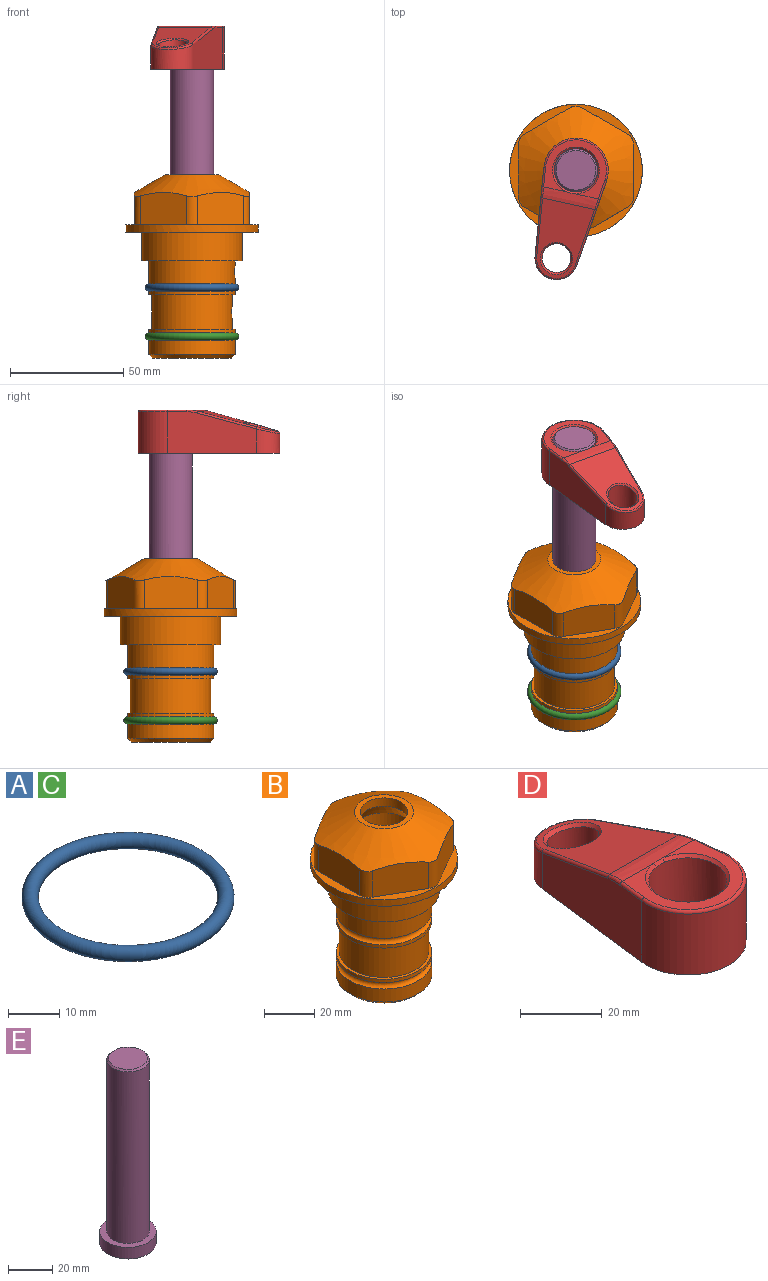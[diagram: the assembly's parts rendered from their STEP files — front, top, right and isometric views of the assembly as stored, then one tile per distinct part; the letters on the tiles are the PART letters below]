
ASSEMBLY  parts=5 mates=4
PART A: 1 faces, bbox 44.7x44.7x3.2 mm
  f0: torus R=19.05mm, axis (0,0,1), area 1193.9mm2
PART B: 36 faces, bbox 58.7x58.7x81 mm
  f0: cylinder r=17.78mm len=35.56mm, axis (0,0,1), area 1670.8mm2, adj f23,f24,f31
  f1: cylinder r=19.05mm len=38.1mm, axis (0,0,1), area 1191.9mm2, adj f26,f27,f30
  f2: plane 58.66x58.66mm, normal (0,0,-1), area 1150.6mm2, adj f3,f28
  f3: cylinder r=29.33mm len=58.66mm, axis (0,0,-1), area 585.1mm2, adj f2,f4
  f4: plane 58.66x58.66mm, normal (0,0,1), area 475.9mm2, adj f3,f5,f6,f7,f8,f9,f10,f11
  f5: plane 20.32x14.34mm, normal (-0.5,0.87,0), area 324.4mm2, adj f4,f15,f16,f17
  f6: plane 20.32x14.34mm, normal (0.5,0.87,0), area 324.4mm2, adj f4,f14,f15,f17
  f7: plane 23.48x14.34mm, normal (1,0,0), area 324.4mm2, adj f4,f13,f14,f17
  f8: plane 20.32x14.34mm, normal (0.5,-0.87,0), area 324.4mm2, adj f4,f12,f13,f17
  f9: plane 20.32x14.34mm, normal (-0.5,-0.87,0), area 324.4mm2, adj f4,f11,f12,f17
  f10: plane 23.48x14.34mm, normal (-1,0,0), area 324.4mm2, adj f4,f11,f16,f17
  f11: cylinder r=5.08mm len=12.85mm, axis (0,0,-1), area 67.2mm2, adj f4,f9,f10,f17
  f12: cylinder r=5.08mm len=12.85mm, axis (0,0,-1), area 67.2mm2, adj f4,f8,f9,f17
  f13: cylinder r=5.08mm len=12.85mm, axis (0,0,-1), area 67.2mm2, adj f4,f7,f8,f17
  f14: cylinder r=5.08mm len=12.85mm, axis (0,0,-1), area 67.2mm2, adj f4,f6,f7,f17
  f15: cylinder r=5.08mm len=12.85mm, axis (0,0,-1), area 67.2mm2, adj f4,f5,f6,f17
  f16: cylinder r=5.08mm len=12.85mm, axis (0,0,-1), area 67.2mm2, adj f4,f5,f10,f17
  f17: cone r=11.73mm half-angle=60deg, axis (0,0,-1), area 2071.8mm2, adj f5,f6,f7,f8,f9,f10,f11,f12
  f18: plane 23.46x23.46mm, normal (0,0,1), area 147.4mm2, adj f17,f35
  f19: plane 34.93x34.93mm, normal (0,0,-1), area 958mm2, adj f29
  f20: cylinder r=19.05mm len=38.1mm, axis (0,0,1), area 760.1mm2, adj f21,f29
  f21: torus R=19.05mm, axis (0,0,1), area 565.3mm2, adj f20,f22
  f22: cylinder r=19.05mm len=38.1mm, axis (0,0,1), area 190mm2, adj f21,f23
  f23: plane 38.1x38.1mm, normal (0,0,1), area 146.9mm2, adj f0,f22
  f24: plane 38.1x38.1mm, normal (0,0,-1), area 146.9mm2, adj f0,f25
  f25: cylinder r=19.05mm len=38.1mm, axis (0,0,1), area 190mm2, adj f24,f26
  f26: torus R=19.05mm, axis (0,0,1), area 565.3mm2, adj f1,f25
  f27: plane 44.45x44.45mm, normal (0,0,-1), area 411.7mm2, adj f1,f28
  f28: cylinder r=22.23mm len=44.45mm, axis (0,0,1), area 1773.5mm2, adj f2,f27
  f29: cone r=19.05mm half-angle=45deg, axis (0,0,1), area 257.5mm2, adj f19,f20
  f30: cylinder r=3.17mm len=6.75mm, axis (-1,0,0), area 128mm2, adj f1,f33
  f31: cylinder r=3.17mm len=6.35mm, axis (-1,0,0), area 102.5mm2, adj f0,f33
  f32: plane 25.4x25.4mm, normal (0,0,1), area 506.7mm2, adj f33
  f33: cylinder r=12.7mm len=66.42mm, axis (0,0,-1), area 5236.2mm2, adj f30,f31,f32,f34
  f34: cone r=9.53mm half-angle=30deg, axis (0,0,-1), area 443.4mm2, adj f33,f35
  f35: cylinder r=9.53mm len=19.05mm, axis (0,0,-1), area 240.9mm2, adj f18,f34
PART C: same geometry as A
PART D: 31 faces, bbox 31.7x65.5x19.8 mm
  f0: plane 39.12x18.26mm, normal (0.99,0.12,0), area 612.2mm2, adj f1,f4,f7,f11,f13,f15
  f1: cylinder r=9.53mm len=18.91mm, axis (0,0,-1), area 296.1mm2, adj f0,f2,f7,f17
  f2: plane 39.12x18.26mm, normal (-0.99,0.12,0), area 612.2mm2, adj f1,f4,f7,f12,f14,f16
  f3: cylinder r=6.35mm len=12.7mm, axis (0,0,-1), area 362.4mm2, adj f7,f18
  f4: cylinder r=14.29mm len=28.58mm, axis (0,0,-1), area 882.2mm2, adj f0,f2,f7,f10
  f5: cylinder r=9.53mm len=19.05mm, axis (0,0,-1), area 1092.6mm2, adj f7,f19,f20
  f6: plane 26.99x23.69mm, normal (0,0,1), area 216.2mm2, adj f9,f10,f11,f12,f19
  f7: plane 63.5x28.58mm, normal (0,0,-1), area 661.8mm2, adj f0,f1,f2,f3,f4,f5,f22,f23
  f8: plane 33.52x23.6mm, normal (0,0.26,0.97), area 486mm2, adj f9,f15,f16,f17,f18
  f9: cylinder r=19.05mm len=24.72mm, axis (1,0,0), area 120.4mm2, adj f6,f8,f13,f14,f20
  f10: torus R=13.49mm, axis (0,0,1), area 59mm2, adj f4,f6,f11,f12
  f11: cylinder r=0.79mm len=8.67mm, axis (0.12,-0.99,0), area 10.8mm2, adj f0,f6,f10,f13
  f12: cylinder r=0.79mm len=8.67mm, axis (0.12,0.99,0), area 10.8mm2, adj f2,f6,f10,f14
  f13: bspline ~4.95x1.42mm, area 6.1mm2, adj f0,f9,f11,f15
  f14: bspline ~4.95x1.42mm, area 6.1mm2, adj f2,f9,f12,f16
  f15: cylinder r=0.79mm len=25.95mm, axis (0.12,-0.96,0.26), area 32.9mm2, adj f0,f8,f13,f17
  f16: cylinder r=0.79mm len=25.95mm, axis (0.12,0.96,-0.26), area 32.9mm2, adj f2,f8,f14,f17
  f17: bspline ~18.91x8.38mm, area 30mm2, adj f1,f8,f15,f16
  f18: bspline ~14.29x14.29mm, area 48.3mm2, adj f3,f8
  f19: cone r=9.53mm half-angle=45deg, axis (0,0,1), area 66.5mm2, adj f5,f6,f20
  f20: bspline ~3.22x0.96mm, area 3.5mm2, adj f5,f9,f19
  f21: plane 2.75x2.72mm, normal (0,0,-1), area 2.9mm2, adj f23,f25,f28
  f22: plane 23.05x15.88mm, normal (-0.99,-0.12,0), area 323.6mm2, adj f7,f25,f26,f27,f28,f29
  f23: plane 23.05x15.88mm, normal (0.99,-0.12,0), area 323.6mm2, adj f7,f21,f25,f27,f28,f30
  f24: cylinder r=9.53mm len=10.69mm, axis (0,0,-1), area 114.7mm2, adj f7,f27,f29,f30
  f25: cylinder r=12.7mm len=20.59mm, axis (0,0,-1), area 381.1mm2, adj f7,f21,f22,f23,f26,f28
  f26: plane 2.75x2.72mm, normal (0,0,-1), area 2.9mm2, adj f22,f25,f28
  f27: plane 19.72x18.37mm, normal (0,-0.26,-0.97), area 291.8mm2, adj f22,f23,f24,f28,f29,f30
  f28: cylinder r=15.88mm len=19.92mm, axis (1,0,0), area 54.8mm2, adj f21,f22,f23,f25,f26,f27
  f29: cylinder r=1.59mm len=11mm, axis (0,0,-1), area 34.7mm2, adj f7,f22,f24,f27
  f30: cylinder r=1.59mm len=11mm, axis (0,0,-1), area 34.7mm2, adj f7,f23,f24,f27
PART E: 6 faces, bbox 25.4x25.4x101.6 mm
  f0: plane 17.46x17.46mm, normal (0,0,1), area 239.5mm2, adj f5
  f1: plane 25.4x25.4mm, normal (0,0,-1), area 506.7mm2, adj f2
  f2: cylinder r=12.7mm len=25.4mm, axis (0,0,1), area 506.7mm2, adj f1,f3
  f3: plane 25.4x25.4mm, normal (0,0,1), area 221.7mm2, adj f2,f4
  f4: cylinder r=9.53mm len=94.46mm, axis (0,0,1), area 5653mm2, adj f3,f5
  f5: cone r=8.73mm half-angle=45deg, axis (0,0,-1), area 64.4mm2, adj f0,f4
PLACE A at identity
PLACE B at identity fixed
PLACE C t=(0,0,-21.59)mm
PLACE D rot(axis=(0,0,1),167.5deg) t=(0,0,27.55)mm
PLACE E rot(axis=(0,0,1),167.5deg) t=(0,0,27.55)mm
MATE fastened D.f4 <-> E.f2  axis (0,0,1) through (0,0,91.05)mm
MATE fastened C.f0 <-> B.f0  axis (0,0,1) through (0,0,-46.1)mm
MATE fastened A.f0 <-> B.f0  axis (0,0,1) through (0,0,-24.51)mm
MATE cylindrical E.f2 <-> B.f0  axis (0,0,-1) through (0,0,-10.55)mm
